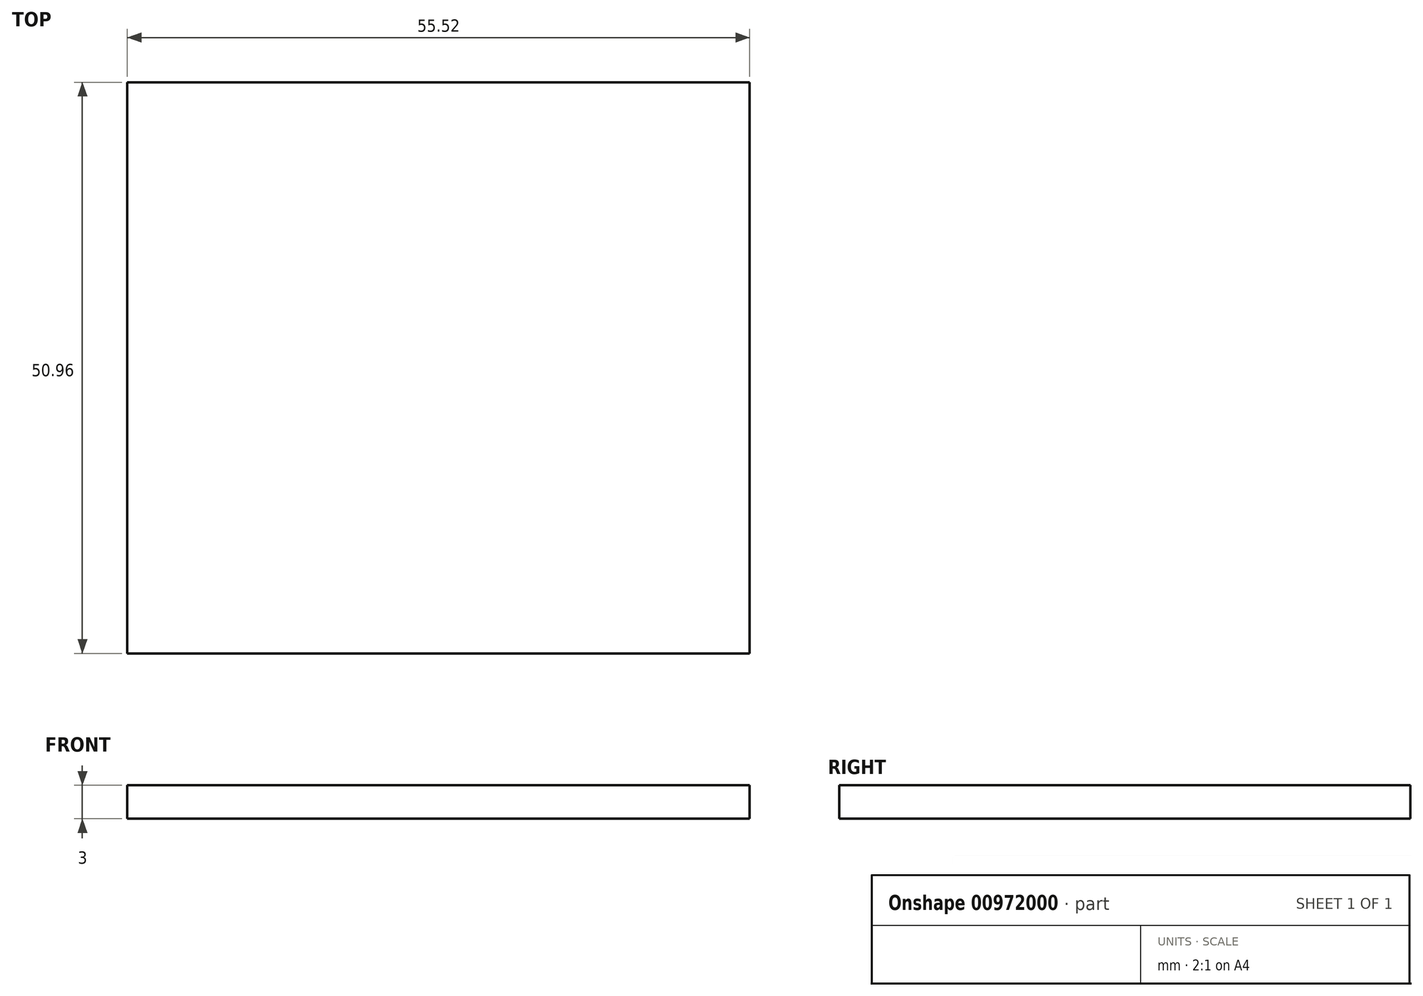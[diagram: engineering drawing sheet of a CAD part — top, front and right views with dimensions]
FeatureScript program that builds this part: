
annotation { "Feature Type Name" : "Feature", "Feature Type Description" : "" }
export const myFeature = defineFeature(function(context is Context, id is Id, definition is map)
    precondition{}
    {
        {
            var Q0;
            Q0=qCreatedBy(makeId("Top.planeOp"),FACE);
            var sketch = newSketch(context, id + "F0", { "sketchPlane" : qUnion([Q0])});
            skLineSegment(sketch, "E0.bottom", {"start": v(27.76, -25.47) * mm, "end": v(-27.76, -25.47) * mm});
            skLineSegment(sketch, "E0.top", {"start": v(27.76, 25.48) * mm, "end": v(-27.76, 25.48) * mm});
            skLineSegment(sketch, "E0.left", {"start": v(27.76, -25.47) * mm, "end": v(27.76, 25.48) * mm});
            skLineSegment(sketch, "E0.right", {"start": v(-27.76, -25.47) * mm, "end": v(-27.76, 25.47) * mm});
            skPoint(sketch, "E0.middle", {"position": v(0, 0) * mm});
            skSolve(sketch);
        }
        {
            var Q0;
            Q0 = qSketchRegion(id + "F0", true);
            extrude(context, id + "F1", {"entities" : qUnion([Q0]), "depth" : 3 * mm, "offsetDistance" : 25 * mm});
        }
    });
